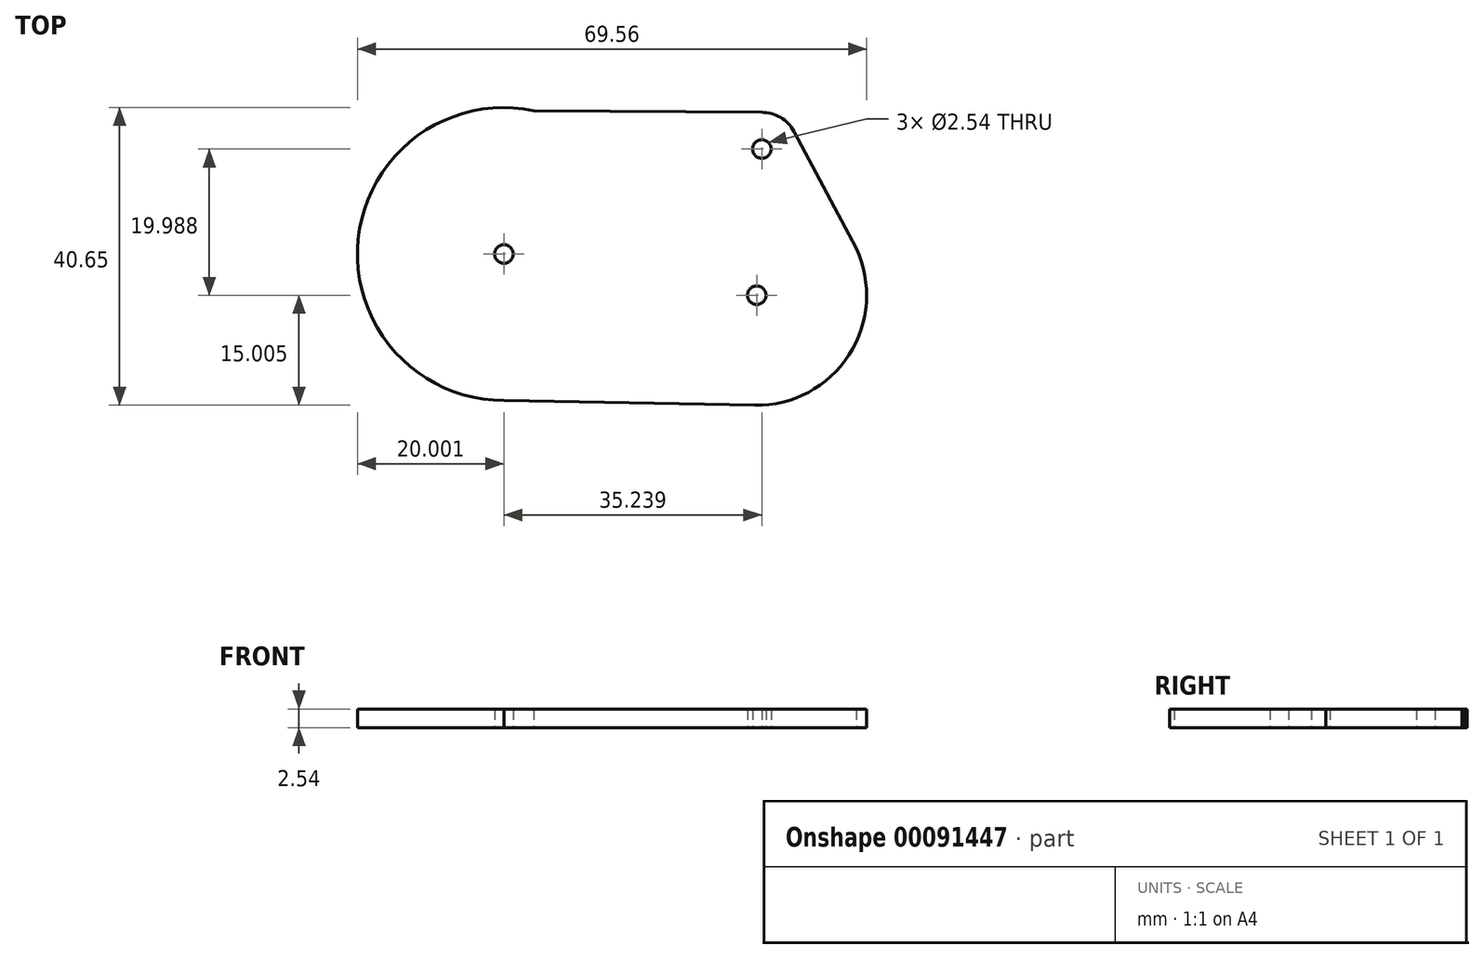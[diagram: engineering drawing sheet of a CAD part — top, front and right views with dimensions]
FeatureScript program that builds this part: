
annotation { "Feature Type Name" : "Feature", "Feature Type Description" : "" }
export const myFeature = defineFeature(function(context is Context, id is Id, definition is map)
    precondition{}
    {
        {
            var Q0;
            Q0=qCreatedBy(makeId("Top.planeOp"),FACE);
            var sketch = newSketch(context, id + "F0", { "sketchPlane" : qUnion([Q0])});
            skCircle(sketch, "E0", {"center": v(-35.24, -5.02) * mm, "radius": 1.27 * mm});
            skCircle(sketch, "E1", {"center": v(-0.7, -10.67) * mm, "radius": 1.27 * mm});
            skCircle(sketch, "E2", {"center": v(0, 9.32) * mm, "radius": 1.27 * mm});
            skLineSegment(sketch, "E3", {"start": v(-31.17, 14.56) * mm, "end": v(0, 14.32) * mm});
            skLineSegment(sketch, "E4", {"start": v(-35.24, -25.02) * mm, "end": v(-0.98, -25.66) * mm});
            skLineSegment(sketch, "E5", {"start": v(4.4, 11.7) * mm, "end": v(12.9, -4.29) * mm});
            skArc(sketch, "E6", {"start": v(-31.17, 14.56) * mm, "mid": v(-55.13, -2.98) * mm, "end": v(-35.24, -25.02) * mm});
            skArc(sketch, "E7", {"start": v(4.4, 11.7) * mm, "mid": v(2.56, 13.63) * mm, "end": v(0, 14.32) * mm});
            skArc(sketch, "E8", {"start": v(-0.98, -25.66) * mm, "mid": v(11.9, -18.83) * mm, "end": v(12.9, -4.29) * mm});
            skSolve(sketch);
        }
        {
            var Q0;
            Q0=makeQuery(id+"F0.imprint","IMPRINT",FACE,{"disambiguationData":[TD([[makeQuery(id+"F0.imprint","IMPRINT",EDGE,{"derivedFrom":sQuery(id+"F0.wireOp",EDGE,"Ah2MPpm2-s986-neK9-2Ifx-1U58amI6LP6V")}),1.0]])]});
            var Q1;
            Q1=makeQuery(id+"F0.imprint","IMPRINT",FACE,{"disambiguationData":[TD([[makeQuery(id+"F0.imprint","IMPRINT",EDGE,{"derivedFrom":sQuery(id+"F0.wireOp",EDGE,"E1")}),-1.0]])]});
            var Q2;
            Q2=makeQuery(id+"F0.imprint","IMPRINT",FACE,{"disambiguationData":[TD([[makeQuery(id+"F0.imprint","IMPRINT",EDGE,{"derivedFrom":sQuery(id+"F0.wireOp",EDGE,"OgKqgtMx-VOxY-8Qf5-juZE-eBjJ457vBLRb")}),1.0]])]});
            extrude(context, id + "F1", {"entities" : qUnion([Q0, Q1, Q2]), "depth" : 2.54 * mm});
        }
    });
